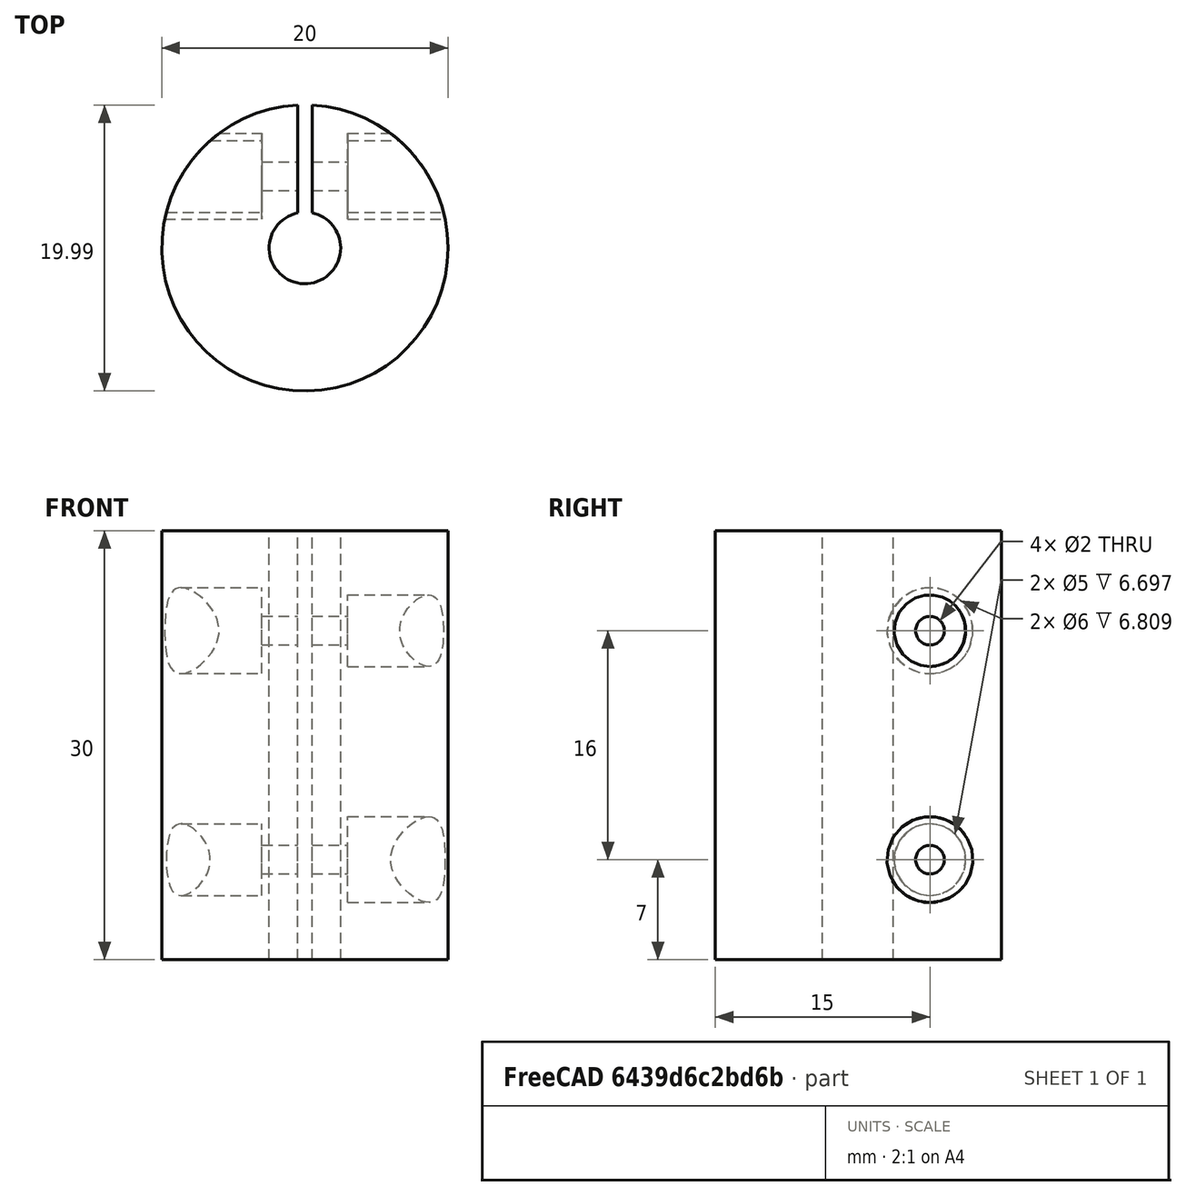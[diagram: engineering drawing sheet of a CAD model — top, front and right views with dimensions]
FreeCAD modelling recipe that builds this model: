
FCSTD DOCUMENT
Label: raccord moteur 5
objects: Part::Cylinder×8, Part::Cut×8, Part::Box×1
note: 17 computed .brp shape members not serialized (recipe doc carries the construction recipe); baked Part::Feature solids carry a one-line shape summary decoded from their .brp

FEATURE [Part::Cylinder] Cylinder001  label="tron centre 5"
  Angle = 360
  Height = 30
  Radius = 2.5
FEATURE [Part::Cylinder] Cylinder002  label="pieces global"
  Angle = 360
  Height = 30
  Radius = 10
FEATURE [Part::Box] Box  label="fente 1mm"
  Height = 30
  Length = 1
  Placement = pos=(-0.5,0,0) rot=(0,0,1;0rad)
  Width = 11
FEATURE [Part::Cylinder] Cylinder  label=" trou vis haut"
  Angle = 360
  Height = 20
  Placement = pos=(-10,5,23) rot=(0,1,0;1.5708rad)
  Radius = 1
FEATURE [Part::Cylinder] Cylinder003  label="trou vis bas"
  Angle = 360
  Height = 20
  Placement = pos=(-10,5,7) rot=(0,1,0;1.5708rad)
  Radius = 1
FEATURE [Part::Cylinder] Cylinder004001  label="Trou tete bg"
  Angle = 360
  Height = 7
  Placement = pos=(-10,5,7) rot=(0,1,0;1.5708rad)
  Radius = 2.5
FEATURE [Part::Cylinder] Cylinder004  label="Trou tete bd"
  Angle = 360
  Height = 7
  Placement = pos=(3,5,7) rot=(0,1,0;1.5708rad)
  Radius = 3
FEATURE [Part::Cylinder] Cylinder004002  label="Trou tete hg"
  Angle = 360
  Height = 7
  Placement = pos=(3,5,23) rot=(0,1,0;1.5708rad)
  Radius = 2.5
FEATURE [Part::Cylinder] Cylinder004002001  label="Trou tete hg001"
  Angle = 360
  Height = 7
  Placement = pos=(-10,5,23) rot=(0,1,0;1.5708rad)
  Radius = 3
FEATURE [Part::Cut] Cut
  Base = -> Cylinder002
  Tool = -> Cylinder001
FEATURE [Part::Cut] Cut001
  Base = -> Cut
  Tool = -> Cylinder004002001
FEATURE [Part::Cut] Cut002
  Base = -> Cut001
  Tool = -> Cylinder004002
FEATURE [Part::Cut] Cut003
  Base = -> Cut002
  Tool = -> Cylinder004
FEATURE [Part::Cut] Cut004
  Base = -> Cut003
  Tool = -> Cylinder004001
FEATURE [Part::Cut] Cut005
  Base = -> Cut004
  Tool = -> Cylinder003
FEATURE [Part::Cut] Cut006
  Base = -> Cut005
  Tool = -> Cylinder
FEATURE [Part::Cut] Cut007
  Base = -> Cut006
  Tool = -> Box
